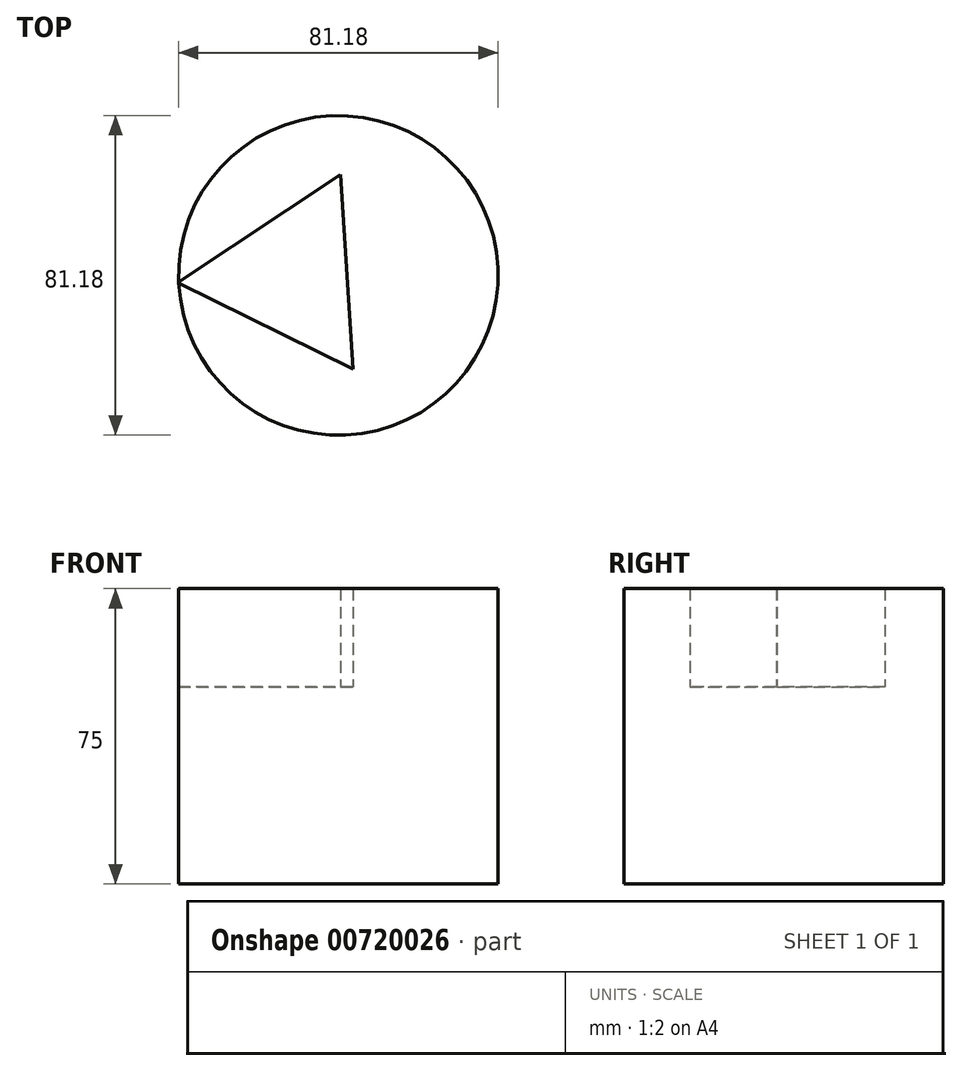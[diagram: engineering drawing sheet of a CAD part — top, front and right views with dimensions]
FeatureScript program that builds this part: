
annotation { "Feature Type Name" : "Feature", "Feature Type Description" : "" }
export const myFeature = defineFeature(function(context is Context, id is Id, definition is map)
    precondition{}
    {
        {
            var Q0;
            Q0=qCreatedBy(makeId("Top.planeOp"),FACE);
            var sketch = newSketch(context, id + "F0", { "sketchPlane" : qUnion([Q0])});
            skCircle(sketch, "E0", {"center": v(0, 0) * mm, "radius": 40.6 * mm});
            skSolve(sketch);
        }
        {
            var Q0;
            Q0=makeQuery(id+"F0.imprint","IMPRINT",FACE,{"disambiguationData":[TD([[makeQuery(id+"F0.imprint","IMPRINT",EDGE,{"derivedFrom":sQuery(id+"F0.wireOp",EDGE,"E0")}),1.0]])]});
            var Q1;
            Q1=sQuery(id+"F0.wireOp",EDGE,"E0");
            extrude(context, id + "F1", {"entities" : qUnion([Q0]), "surfaceEntities" : qUnion([Q1]), "depth" : 50 * mm, "offsetDistance" : 25 * mm});
        }
        {
            var Q0;
            Q0=makeQuery(id+"F1.opExtrude","CAP_FACE",FACE,{"disambiguationData":[OSD([sQuery(id+"F0.wireOp",EDGE,"E0")])],"isStart":false});
            var sketch = newSketch(context, id + "F2", { "sketchPlane" : qUnion([Q0])});
            skSolve(sketch);
        }
        {
            var Q0;
            Q0=makeQuery(id+"F2.imprint","IMPRINT",FACE,{"disambiguationData":[TD([[makeQuery(id+"F2.imprint","IMPRINT",EDGE,{"derivedFrom":makeQuery(id+"F1.opExtrude","CAP_EDGE",EDGE,{"disambiguationData":[OSD([sQuery(id+"F0.wireOp",EDGE,"E0")])],"isStart":false})}),1.0]])]});
            var sketch = newSketch(context, id + "F3", { "sketchPlane" : qUnion([Q0])});
            skCircle(sketch, "E1.cCircle", {"center": v(-12.16, 0) * mm, "radius": 14.31 * mm, "construction": true});
            skLineSegment(sketch, "E1.0", {"start": v(-40.73, -1.82) * mm, "end": v(0.54, 25.65) * mm});
            skLineSegment(sketch, "E1.1", {"start": v(0.54, 25.65) * mm, "end": v(3.7, -23.83) * mm});
            skLineSegment(sketch, "E1.2", {"start": v(3.7, -23.83) * mm, "end": v(-40.73, -1.82) * mm});
            skPoint(sketch, "E1.0.midPoint", {"position": v(-20.1, 11.91) * mm});
            skSolve(sketch);
        }
        {
            var Q0;
            {var subQ0=sQuery(id+"F3.wireOp",EDGE,"E1.1");Q0=makeQuery(id+"F3.imprint","IMPRINT",FACE,{"disambiguationData":[TD([[makeQuery(id+"F3.imprint","IMPRINT",EDGE,{"derivedFrom":subQ0}),1.0]])]});}
            extrude(context, id + "F4", {"entities" : qUnion([Q0]), "operationType" : NewBodyOperationType.ADD, "depth" : 25 * mm, "offsetDistance" : 25 * mm});
        }
    });
